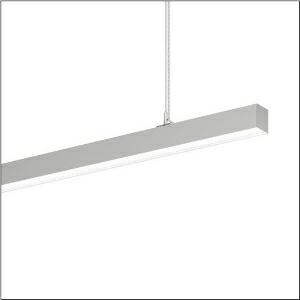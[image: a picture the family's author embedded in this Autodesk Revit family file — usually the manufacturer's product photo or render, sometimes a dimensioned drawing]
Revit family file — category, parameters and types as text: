
# Revit family: silica_r__21_51mx33tctds_657e
name_source: partatom
category: Lighting Fixtures
units: mm (PartAtom-declared; Revit-internal decimal feet)

## family parameters
Cut with Voids When Loaded = No
Host = Face
Light Source = No
Part Type = Normal
Room Calculation Point = No
Round Connector Dimension = Use Diameter
Shared = No

## types (1)
- --- (1 x LED, 14340 lm, 134.7 W, 6500K)
    Apparent Load = 135 VA
    CIE Flux Codes = 78 96 99 56 100
    Color Rendering = 80
    Color Temperature = 6500K
    Default Elevation = 1800 mm
    Description = Silica® 21, office luminaire, primary optical cover: prismatic diffuser, of PMMA, CAT 2 (L<= 3000cd/m²), light emission: direct/indirect distribution, primary light characteristic: symmetric, installation type: suspended mounting, LED, rated luminous flux: 14.340lm, luminous efficacy: 101lm/W, light colour: 8tw, colour temperature: 2700..6500K, control gear: ECG DALI, with terminal, 3+2-pole, max. 2.5mm², mains connection: 220..240V, AC, 50/60Hz, rated input power: 141.4W, luminaire housing, of aluminium, metallic grey (RAL 9006), length: 3.004mm, width: 53mm, height: 53mm, protection rating (complete): IP20, insulation class (complete): insulation class I (protective earthing), certification: CE, permissible operating ambient temperature: 0..+35°C, standard: EN 50419, packaging unit: 1 piece
    Height = 53 mm
    Lamp = 1 x LED
    Lamp Light Flux = 14340 lm
    Lamp Power = 134.7 W
    Lamp count = 1
    Length = 3004 mm
    Luminous efficacy = 106 lm/W
    Manufacturer = Siteco
    ModVariant = No
    Model = 51MX33TCTDS
    Mounting Place = Ceiling
    Mounting Type = Pendant
    Number of Poles = 1
    OnlyDefault = Yes
    Power Factor = 1
    Product Name = Silica® 21
    Product group = office luminaire | ceiling pendant
    ProductGroupID = 905
    Protection Class = Protection class I
    Protection Degree = IP 20
    RLX_Detail_Level = 1
    RlxData = <blob elided: 20109 chars, md5=edd0c432>
    Socket = socket
    Standby Power = 0 W
    System Light Flux = 14340 lm
    System Power = 135 W
    Type Comments = individual setting
    Type Image = l_1251727.jpg
    URL = http://relux.com
    VarID = @adj_045825
    Voltage = 0 V
    Weight = 0.00 kg
    Width = 53 mm

## geometry (parser evidence)
native form markers: Blend x4, Sweep x10
no freeform markers — native parametric forms only
